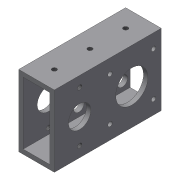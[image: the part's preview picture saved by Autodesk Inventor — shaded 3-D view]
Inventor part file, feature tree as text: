
AUTODESK INVENTOR PART (.ipt)
format: ipt  version: 2018 (Build 220112000, 112)  size: 180,736 bytes
history: native  units: mm
features: sketch x6, hole x4, extrude x3, other x3, shell x1, reference x1
ambient origin geometry x8: Origin, YZ Plane, XZ Plane, XY Plane, X Axis, Y Axis, Z Axis, Center Point
bodies: Solid1 (feature_tree)
feature tree (18):
  extrude  "Extrusion1"  Depth=25.4mm
  shell  "Shell1"  Thickness=76.2mm
  sketch  "Sketch2"  dims[d4=3.175mm d5=31.0mm]
  hole  "Hole1"  [1 undecoded]
  hole  "Hole2"  [1 undecoded]
  extrude  "Extrusion2"  Depth=8.0mm
  extrude  "Extrusion3"  Depth=50.8mm
  hole  "Hole4"  [1 undecoded]
  hole  "Hole5"  [1 undecoded]
  sketch  "Sketch1"  dims[d0=50.8mm d1=25.4mm d2=76.2mm d3=0.0mm]
  sketch  "Sketch3"  dims[d6=31.0mm d7=21.0mm]
  sketch  "Sketch4"  dims[d8=3.2mm d9=6.0mm d10=7.5mm d11=5.0mm d12=90.0deg d13=8.0mm d14=20.594885mm]
  sketch  "Sketch6"  dims[d15=10.0mm d16=6.0mm d17=6.5mm d18=3.0mm d19=90.0deg d20=8.0mm d21=20.594885mm d22=23.0mm]
  sketch  "Sketch7"  dims[d23=50.8mm d24=0.0mm d25=16.0mm d26=18.0mm d27=50.8mm d28=0.0mm d40=3.242mm d41=100.0mm d42=6.5mm d43=3.0mm d44=90.0deg d45=11.8mm d46=20.594885mm d47=36.0mm d48=3.242mm d49=100.0mm d50=6.5mm d51=3.0mm d52=90.0deg d53=11.8mm d54=20.594885mm d55=50.8mm]
  reference  "Reference1"
  parser-record x1  (decoder bookkeeping rows leaked as tree rows — omitted from the tree; the rows remain in map.json)
  other  "AMR_Transm.iam"
  other  "7804K147_STAINLESS STEEL BALL BEARING:2"
note: 4 required parameter values undecoded (feature->parameter linkage not recoverable at this tier; creation-order binding heuristic only, values carry confidence <= 0.55)
note: 1 file-system path scrubbed to <path> (originals preserved in map.json)
